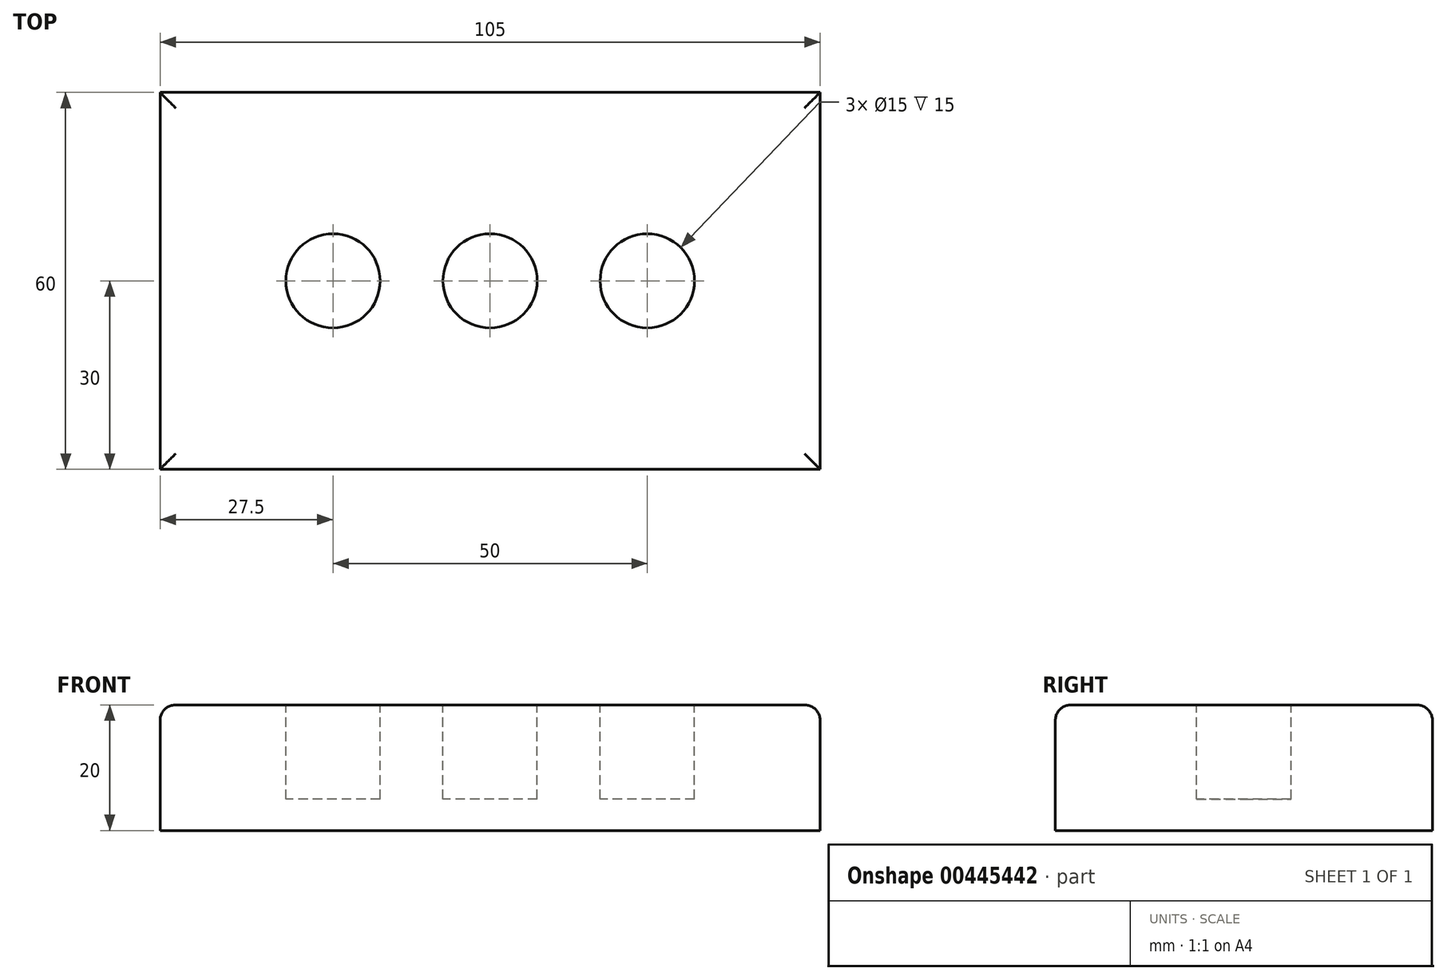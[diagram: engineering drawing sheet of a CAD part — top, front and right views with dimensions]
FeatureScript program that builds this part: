
annotation { "Feature Type Name" : "Feature", "Feature Type Description" : "" }
export const myFeature = defineFeature(function(context is Context, id is Id, definition is map)
    precondition{}
    {
        {
            var Q0;
            Q0=qCreatedBy(makeId("Top.planeOp"),FACE);
            var sketch = newSketch(context, id + "F0", { "sketchPlane" : qUnion([Q0])});
            skLineSegment(sketch, "E0.bottom", {"start": v(52.5, 30) * mm, "end": v(-52.5, 30) * mm});
            skLineSegment(sketch, "E0.top", {"start": v(52.5, -30) * mm, "end": v(-52.5, -30) * mm});
            skLineSegment(sketch, "E0.left", {"start": v(52.5, 30) * mm, "end": v(52.5, -30) * mm});
            skLineSegment(sketch, "E0.right", {"start": v(-52.5, 30) * mm, "end": v(-52.5, -30) * mm});
            skPoint(sketch, "E0.middle", {"position": v(0, 0) * mm});
            skSolve(sketch);
        }
        {
            var Q0;
            Q0=makeQuery(id+"F0.imprint","IMPRINT",FACE,{"disambiguationData":[TD([[makeQuery(id+"F0.imprint","IMPRINT",EDGE,{"derivedFrom":sQuery(id+"F0.wireOp",EDGE,"E0.bottom")}),1.0]])]});
            extrude(context, id + "F1", {"entities" : qUnion([Q0]), "depth" : 20 * mm});
        }
        {
            var Q0;
            Q0=makeQuery(id+"F1.opExtrude","CAP_FACE",FACE,{"disambiguationData":[OSD([sQuery(id+"F0.wireOp",EDGE,"E0.bottom"),sQuery(id+"F0.wireOp",EDGE,"E0.top"),sQuery(id+"F0.wireOp",EDGE,"E0.left"),sQuery(id+"F0.wireOp",EDGE,"E0.right")])],"isStart":false});
            var sketch = newSketch(context, id + "F2", { "sketchPlane" : qUnion([Q0])});
            skCircle(sketch, "E1", {"center": v(0, 0) * mm, "radius": 7.5 * mm});
            skCircle(sketch, "E2", {"center": v(25, 0) * mm, "radius": 7.5 * mm});
            skCircle(sketch, "E3", {"center": v(-25, 0) * mm, "radius": 7.5 * mm});
            skSolve(sketch);
        }
        {
            var Q0;
            Q0=makeQuery(id+"F2.imprint","IMPRINT",FACE,{"disambiguationData":[TD([[makeQuery(id+"F2.imprint","IMPRINT",EDGE,{"derivedFrom":sQuery(id+"F2.wireOp",EDGE,"E3")}),1.0]])]});
            var Q1;
            Q1=makeQuery(id+"F2.imprint","IMPRINT",FACE,{"disambiguationData":[TD([[makeQuery(id+"F2.imprint","IMPRINT",EDGE,{"derivedFrom":sQuery(id+"F2.wireOp",EDGE,"E2")}),1.0]])]});
            var Q2;
            Q2=makeQuery(id+"F2.imprint","IMPRINT",FACE,{"disambiguationData":[TD([[makeQuery(id+"F2.imprint","IMPRINT",EDGE,{"derivedFrom":sQuery(id+"F2.wireOp",EDGE,"E1")}),1.0]])]});
            extrude(context, id + "F3", {"entities" : qUnion([Q0, Q1, Q2]), "operationType" : NewBodyOperationType.REMOVE, "oppositeDirection" : true, "depth" : 15 * mm});
        }
        {
            var Q0;
            Q0=makeQuery(id+"F1.opExtrude","CAP_EDGE",EDGE,{"disambiguationData":[OSD([sQuery(id+"F0.wireOp",EDGE,"E0.right")])],"isStart":false});
            var Q1;
            Q1=makeQuery(id+"F1.opExtrude","CAP_EDGE",EDGE,{"disambiguationData":[OSD([sQuery(id+"F0.wireOp",EDGE,"E0.bottom")])],"isStart":false});
            var Q2;
            Q2=makeQuery(id+"F1.opExtrude","CAP_EDGE",EDGE,{"disambiguationData":[OSD([sQuery(id+"F0.wireOp",EDGE,"E0.left")])],"isStart":false});
            var Q3;
            Q3=makeQuery(id+"F1.opExtrude","CAP_EDGE",EDGE,{"disambiguationData":[OSD([sQuery(id+"F0.wireOp",EDGE,"E0.top")])],"isStart":false});
            fillet(context, id + "F4", {"entities" : qUnion([Q0, Q1, Q2, Q3]), "radius" : 2.5 * mm, "tangentPropagation" : true, "allowEdgeOverflow" : false});
        }
    });
